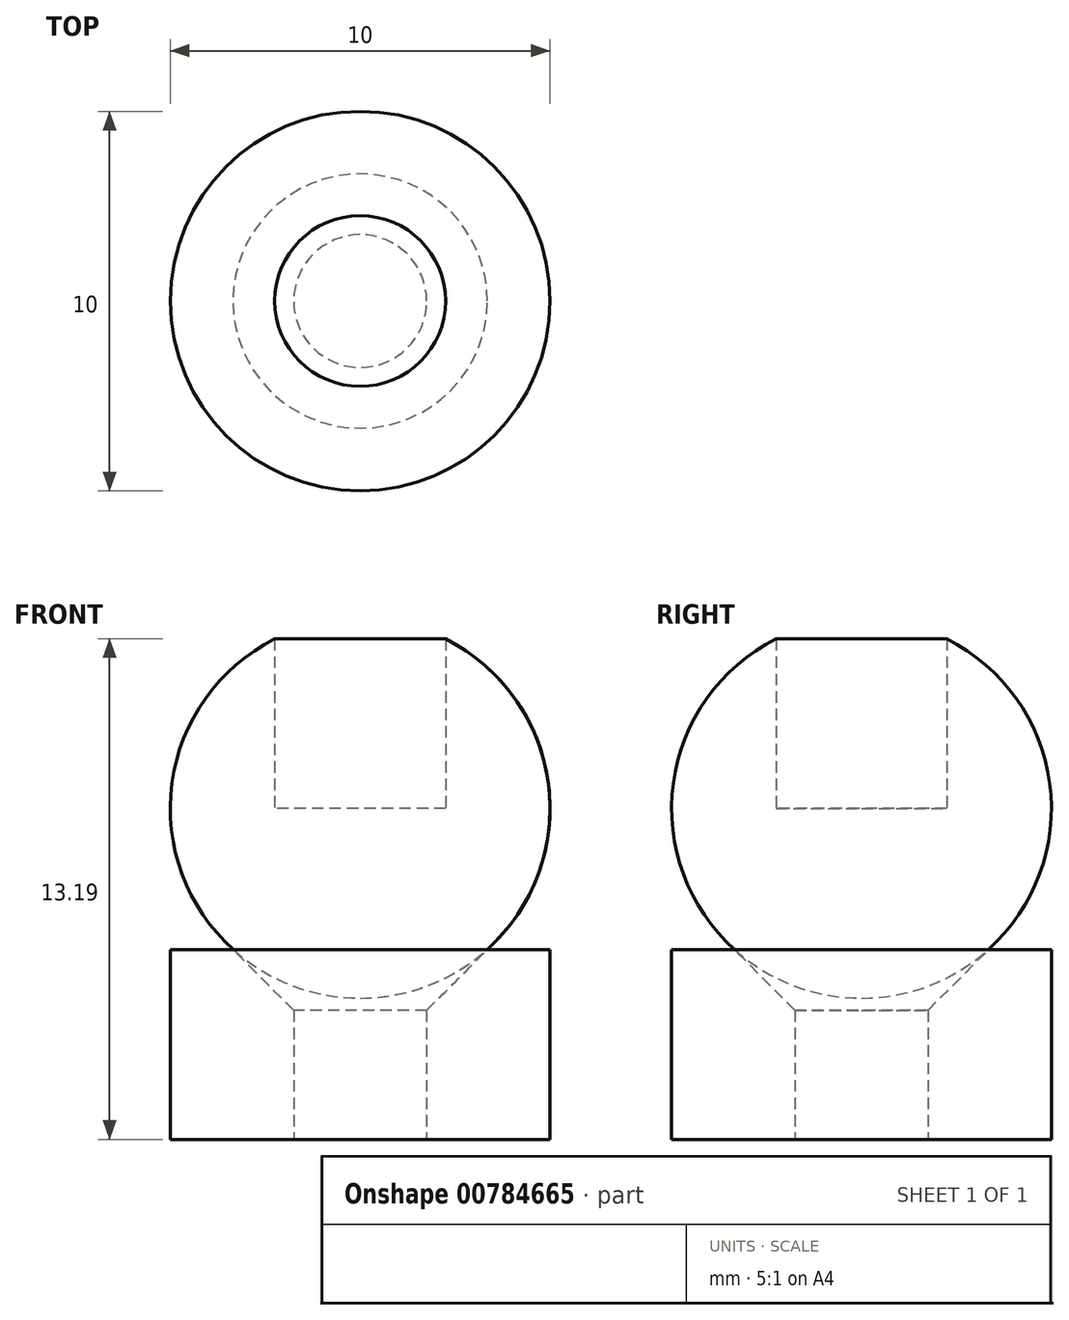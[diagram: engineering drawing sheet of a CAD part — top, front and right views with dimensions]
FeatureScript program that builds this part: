
annotation { "Feature Type Name" : "Feature", "Feature Type Description" : "" }
export const myFeature = defineFeature(function(context is Context, id is Id, definition is map)
    precondition{}
    {
        {
            var Q0;
            Q0=qCreatedBy(makeId("Top.planeOp"),FACE);
            var sketch = newSketch(context, id + "F0", { "sketchPlane" : qUnion([Q0])});
            skCircle(sketch, "E0", {"center": v(0, 0) * mm, "radius": 5 * mm});
            skCircle(sketch, "E1", {"center": v(0, 0) * mm, "radius": 1.75 * mm});
            skSolve(sketch);
        }
        {
            var Q0;
            Q0=qSketchRegion(id+"F0",true);
            extrude(context, id + "F1", {"entities" : qUnion([Q0]), "depth" : 5 * mm, "offsetDistance" : 25 * mm});
        }
        {
            var Q0;
            Q0=makeQuery(id+"F1.opExtrude","CAP_EDGE",EDGE,{"disambiguationData":[OSD([sQuery(id+"F0.wireOp",EDGE,"E1")])],"isStart":false});
            chamfer(context, id + "F2", {"entities" : qUnion([Q0]), "width" : 1.6 * mm, "tangentPropagation" : true});
        }
        {
            var Q0;
            Q0=qCreatedBy(makeId("Top.planeOp"),FACE);
            cPlane(context, id + "F3", {"entities" : qUnion([Q0]), "cplaneType" : CPlaneType.OFFSET, "offset" : 8.72 * mm, "width" : 150 * mm, "height" : 150 * mm});
        }
        {
            var Q0;
            Q0=qCreatedBy(id+"F3.planeOp",FACE);
            var sketch = newSketch(context, id + "F4", { "sketchPlane" : qUnion([Q0])});
            skCircle(sketch, "E2", {"center": v(0, 0) * mm, "radius": 5 * mm});
            skCircle(sketch, "E3", {"center": v(0, 0) * mm, "radius": 2.25 * mm});
            skSolve(sketch);
        }
        {
            var Q0;
            Q0 = qSketchRegion(id + "F4", true);
            var Q1;
            Q1=makeQuery(id+"F4.imprint","IMPRINT",FACE,{"disambiguationData":[TD([[makeQuery(id+"F4.imprint","IMPRINT",EDGE,{"derivedFrom":sQuery(id+"F4.wireOp",EDGE,"E3")}),1.0]])]});
            extrude(context, id + "F5", {"entities" : qUnion([Q0, Q1]), "depth" : 10 * mm, "offsetDistance" : 25 * mm, "symmetric" : true});
        }
        {
            var Q0;
            Q0=makeQuery(id+"F5.opExtrude","SWEPT_FACE",FACE,{"disambiguationData":[OSD([sQuery(id+"F4.wireOp",EDGE,"E2")])]});
            fillet(context, id + "F6", {"entities" : qUnion([Q0]), "radius" : 5 * mm, "tangentPropagation" : true, "allowEdgeOverflow" : false});
        }
        {
            var Q0;
            Q0=makeQuery(id+"F4.imprint","IMPRINT",FACE,{"disambiguationData":[TD([[makeQuery(id+"F4.imprint","IMPRINT",EDGE,{"derivedFrom":sQuery(id+"F4.wireOp",EDGE,"E3")}),1.0]])]});
            extrude(context, id + "F7", {"entities" : qUnion([Q0]), "operationType" : NewBodyOperationType.REMOVE, "depth" : 10 * mm, "offsetDistance" : 25 * mm});
        }
    });
